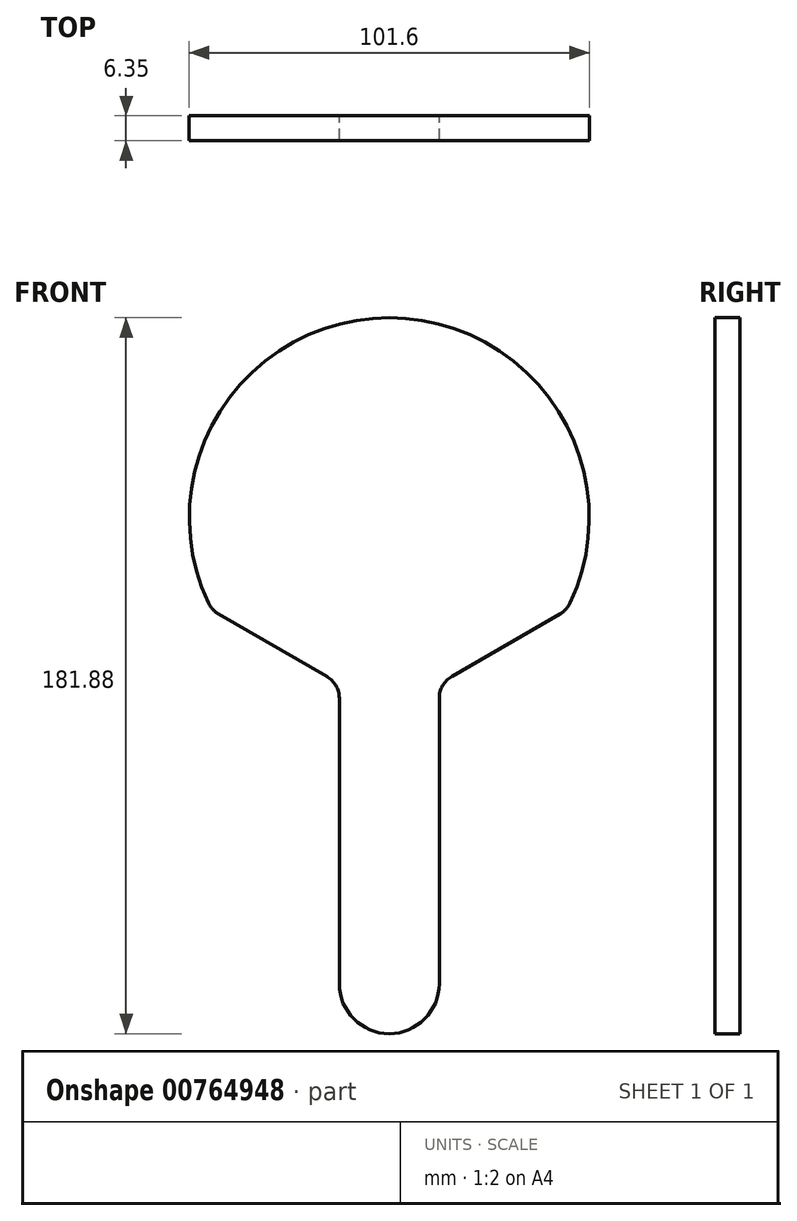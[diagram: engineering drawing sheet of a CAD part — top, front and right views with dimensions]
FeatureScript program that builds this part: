
annotation { "Feature Type Name" : "Feature", "Feature Type Description" : "" }
export const myFeature = defineFeature(function(context is Context, id is Id, definition is map)
    precondition{}
    {
        {
            var Q0;
            Q0=qCreatedBy(makeId("Front.planeOp"),FACE);
            var sketch = newSketch(context, id + "F0", { "sketchPlane" : qUnion([Q0])});
            skFitSpline(sketch, "E0", {"points": [v(-45.43, 10.04) * mm, v(-45.35, 10.36) * mm], "startDerivative": vector(0.07, 0.32) * mm, "endDerivative": vector(0.07, 0.32) * mm});
            skLineSegment(sketch, "E1", {"start": v(22.75, 17.65) * mm, "end": v(22.75, -54.88) * mm});
            skLineSegment(sketch, "E2", {"start": v(48.15, 17.65) * mm, "end": v(48.15, -54.88) * mm});
            skArc(sketch, "E3", {"start": v(22.75, -54.88) * mm, "mid": v(35.45, -67.58) * mm, "end": v(48.15, -54.88) * mm});
            skLineSegment(sketch, "E4", {"start": v(19.58, 23.15) * mm, "end": v(-7.92, 39.03) * mm});
            skLineSegment(sketch, "E5", {"start": v(51.33, 23.15) * mm, "end": v(78.83, 39.03) * mm});
            skArc(sketch, "E6", {"start": v(81.4, 41.82) * mm, "mid": v(35.45, 114.3) * mm, "end": v(-10.48, 41.82) * mm});
            skPoint(sketch, "E7.visualSharp", {"position": v(48.15, 21.32) * mm});
            skArc(sketch, "E7.filletArc", {"start": v(51.33, 23.15) * mm, "mid": v(49, 20.83) * mm, "end": v(48.15, 17.65) * mm});
            skPoint(sketch, "E8.visualSharp", {"position": v(22.75, 21.32) * mm});
            skArc(sketch, "E8.filletArc", {"start": v(22.75, 17.65) * mm, "mid": v(21.9, 20.83) * mm, "end": v(19.58, 23.15) * mm});
            skArc(sketch, "E9.filletArc", {"start": v(78.83, 39.03) * mm, "mid": v(80.32, 40.23) * mm, "end": v(81.4, 41.82) * mm});
            skArc(sketch, "E10.filletArc", {"start": v(-10.48, 41.82) * mm, "mid": v(-9.41, 40.23) * mm, "end": v(-7.92, 39.03) * mm});
            skPoint(sketch, "E11.newPointB", {"position": v(-7.92, 39.03) * mm});
            skSolve(sketch);
        }
        {
            var Q0;
            Q0 = qSketchRegion(id + "F0", true);
            extrude(context, id + "F1", {"entities" : qUnion([Q0]), "depth" : 6.35 * mm, "offsetDistance" : 25.4 * mm});
        }
    });
